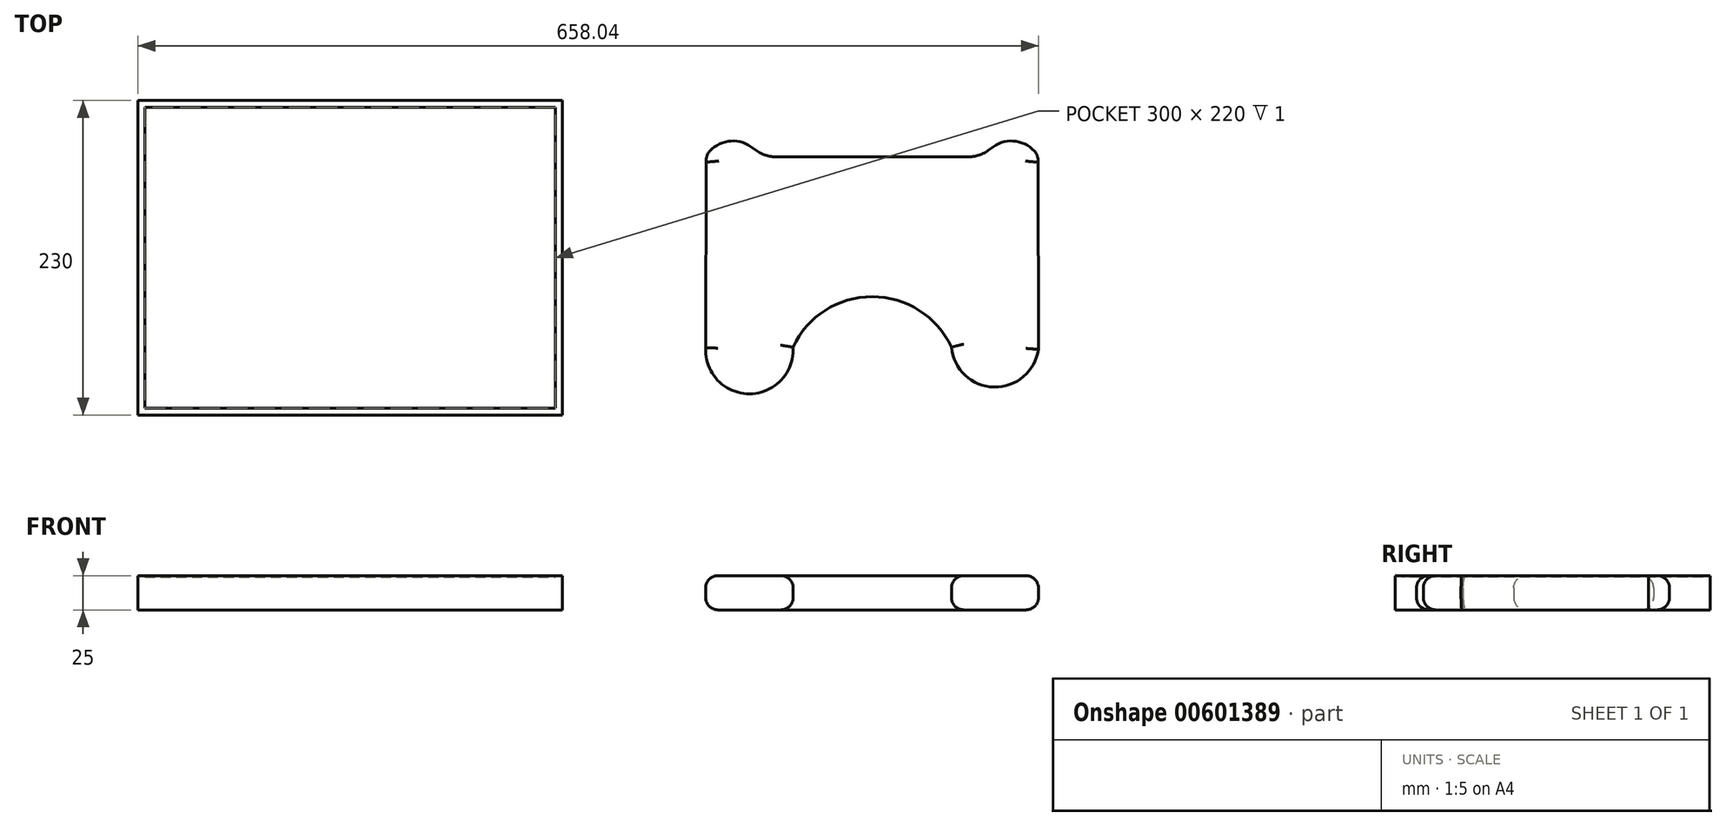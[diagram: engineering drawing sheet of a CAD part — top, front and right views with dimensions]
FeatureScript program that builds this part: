
annotation { "Feature Type Name" : "Feature", "Feature Type Description" : "" }
export const myFeature = defineFeature(function(context is Context, id is Id, definition is map)
    precondition{}
    {
        {
            var Q0;
            Q0=qCreatedBy(makeId("Top.planeOp"),FACE);
            var sketch = newSketch(context, id + "F0", { "sketchPlane" : qUnion([Q0])});
            skLineSegment(sketch, "E0.bottom", {"start": v(-155, 115) * mm, "end": v(155, 115) * mm});
            skLineSegment(sketch, "E0.top", {"start": v(-155, -115) * mm, "end": v(155, -115) * mm});
            skLineSegment(sketch, "E0.left", {"start": v(-155, 115) * mm, "end": v(-155, -115) * mm});
            skLineSegment(sketch, "E0.right", {"start": v(155, 115) * mm, "end": v(155, -115) * mm});
            skLineSegment(sketch, "E1", {"start": v(0, 0) * mm, "end": v(0, 115) * mm, "construction": true});
            skLineSegment(sketch, "E2", {"start": v(0, 0) * mm, "end": v(155, 0) * mm, "construction": true});
            skSolve(sketch);
        }
        {
            var Q0;
            Q0=makeQuery(id+"F0.imprint","IMPRINT",FACE,{"disambiguationData":[TD([[makeQuery(id+"F0.imprint","IMPRINT",EDGE,{"derivedFrom":sQuery(id+"F0.wireOp",EDGE,"E0.bottom")}),-1.0]])]});
            extrude(context, id + "F1", {"entities" : qUnion([Q0]), "depth" : 25 * mm, "offsetDistance" : 25 * mm, "symmetric" : true});
        }
        {
            var Q0;
            Q0=makeQuery(id+"F1.opExtrude","CAP_FACE",FACE,{"disambiguationData":[OSD([sQuery(id+"F0.wireOp",EDGE,"E0.bottom"),sQuery(id+"F0.wireOp",EDGE,"E0.top"),sQuery(id+"F0.wireOp",EDGE,"E0.left"),sQuery(id+"F0.wireOp",EDGE,"E0.right")])],"isStart":false});
            var sketch = newSketch(context, id + "F2", { "sketchPlane" : qUnion([Q0])});
            skLineSegment(sketch, "E3.bottom", {"start": v(-150, 110) * mm, "end": v(150, 110) * mm});
            skLineSegment(sketch, "E3.top", {"start": v(-150, -110) * mm, "end": v(150, -110) * mm});
            skLineSegment(sketch, "E3.left", {"start": v(-150, 110) * mm, "end": v(-150, -110) * mm});
            skLineSegment(sketch, "E3.right", {"start": v(150, 110) * mm, "end": v(150, -110) * mm});
            skSolve(sketch);
        }
        {
            var Q0;
            Q0=makeQuery(id+"F2.imprint","IMPRINT",FACE,{"disambiguationData":[TD([[makeQuery(id+"F2.imprint","IMPRINT",EDGE,{"derivedFrom":sQuery(id+"F2.wireOp",EDGE,"E3.bottom")}),-1.0]])]});
            extrude(context, id + "F3", {"entities" : qUnion([Q0]), "operationType" : NewBodyOperationType.REMOVE, "oppositeDirection" : true, "depth" : 1 * mm, "offsetDistance" : 25 * mm});
        }
        {
            var Q0;
            Q0=qCreatedBy(makeId("Top.planeOp"),FACE);
            var sketch = newSketch(context, id + "F4", { "sketchPlane" : qUnion([Q0])});
            skArc(sketch, "E4", {"start": v(259.83, -65.82) * mm, "mid": v(292, -99.5) * mm, "end": v(323.72, -65.41) * mm});
            skArc(sketch, "E5", {"start": v(439.47, -65.41) * mm, "mid": v(381.6, -28.43) * mm, "end": v(323.72, -65.41) * mm});
            skArc(sketch, "E6", {"start": v(439.47, -65.41) * mm, "mid": v(470.57, -94.54) * mm, "end": v(503.04, -66.95) * mm});
            skArc(sketch, "E7", {"start": v(294.87, 79.85) * mm, "mid": v(278.48, 85.39) * mm, "end": v(262.87, 77.94) * mm});
            skArc(sketch, "E8", {"start": v(500.1, 78.05) * mm, "mid": v(484.51, 85.4) * mm, "end": v(468.2, 79.85) * mm});
            skLineSegment(sketch, "E9", {"start": v(311.2, 73.79) * mm, "end": v(451.88, 73.79) * mm});
            skPoint(sketch, "E10.visualSharp", {"position": v(299.86, 73.79) * mm});
            skArc(sketch, "E10.filletArc", {"start": v(294.87, 79.85) * mm, "mid": v(302.49, 75.35) * mm, "end": v(311.2, 73.79) * mm});
            skPoint(sketch, "E11.visualSharp", {"position": v(463.21, 73.79) * mm});
            skArc(sketch, "E11.filletArc", {"start": v(451.88, 73.79) * mm, "mid": v(460.58, 75.35) * mm, "end": v(468.2, 79.85) * mm});
            skPoint(sketch, "E12.visualSharp", {"position": v(503.21, 73.79) * mm});
            skArc(sketch, "E12.filletArc", {"start": v(502.66, 69.9) * mm, "mid": v(502.3, 74.26) * mm, "end": v(500.1, 78.05) * mm});
            skPoint(sketch, "E13.visualSharp", {"position": v(259.86, 73.79) * mm});
            skArc(sketch, "E13.filletArc", {"start": v(262.87, 77.94) * mm, "mid": v(260.73, 74.24) * mm, "end": v(260.33, 70) * mm});
            skLineSegment(sketch, "E14", {"start": v(502.66, 69.9) * mm, "end": v(503.04, -66.95) * mm});
            skLineSegment(sketch, "E15", {"start": v(260.33, 70) * mm, "end": v(259.83, -65.82) * mm});
            skSolve(sketch);
        }
        {
            var Q0;
            Q0=makeQuery(id+"F4.imprint","IMPRINT",FACE,{"disambiguationData":[TD([[makeQuery(id+"F4.imprint","IMPRINT",EDGE,{"derivedFrom":sQuery(id+"F4.wireOp",EDGE,"E4")}),1.0]])]});
            extrude(context, id + "F5", {"entities" : qUnion([Q0]), "depth" : 25 * mm, "offsetDistance" : 25 * mm, "symmetric" : true});
        }
        {
            var Q0;
            Q0=makeQuery(id+"F5.opExtrude","CAP_EDGE",EDGE,{"disambiguationData":[OSD([sQuery(id+"F4.wireOp",EDGE,"E5")])],"isStart":false});
            var Q1;
            Q1=makeQuery(id+"F5.opExtrude","CAP_EDGE",EDGE,{"disambiguationData":[OSD([sQuery(id+"F4.wireOp",EDGE,"E5")])],"isStart":true});
            var Q2;
            Q2=makeQuery(id+"F5.opExtrude","CAP_EDGE",EDGE,{"disambiguationData":[OSD([sQuery(id+"F4.wireOp",EDGE,"E4")])],"isStart":true});
            var Q3;
            Q3=makeQuery(id+"F5.opExtrude","CAP_EDGE",EDGE,{"disambiguationData":[OSD([sQuery(id+"F4.wireOp",EDGE,"E4")])],"isStart":false});
            var Q4;
            Q4=makeQuery(id+"F5.opExtrude","CAP_EDGE",EDGE,{"disambiguationData":[OSD([sQuery(id+"F4.wireOp",EDGE,"E6")])],"isStart":false});
            var Q5;
            Q5=makeQuery(id+"F5.opExtrude","CAP_EDGE",EDGE,{"disambiguationData":[OSD([sQuery(id+"F4.wireOp",EDGE,"E9")])],"isStart":true});
            var Q6;
            Q6=makeQuery(id+"F5.opExtrude","CAP_EDGE",EDGE,{"disambiguationData":[OSD([sQuery(id+"F4.wireOp",EDGE,"E6")])],"isStart":true});
            var Q7;
            Q7=makeQuery(id+"F5.opExtrude","CAP_EDGE",EDGE,{"disambiguationData":[OSD([sQuery(id+"F4.wireOp",EDGE,"E14")])],"isStart":false});
            var Q8;
            Q8=makeQuery(id+"F5.opExtrude","CAP_EDGE",EDGE,{"disambiguationData":[OSD([sQuery(id+"F4.wireOp",EDGE,"E14")])],"isStart":true});
            var Q9;
            Q9=makeQuery(id+"F5.opExtrude","CAP_EDGE",EDGE,{"disambiguationData":[OSD([sQuery(id+"F4.wireOp",EDGE,"E8")])],"isStart":false});
            var Q10;
            Q10=makeQuery(id+"F5.opExtrude","CAP_EDGE",EDGE,{"disambiguationData":[OSD([sQuery(id+"F4.wireOp",EDGE,"E12.filletArc")])],"isStart":false});
            fillet(context, id + "F6", {"entities" : qUnion([Q0, Q1, Q2, Q3, Q4, Q5, Q6, Q7, Q8, Q9, Q10]), "radius" : 9 * mm, "tangentPropagation" : true, "allowEdgeOverflow" : false});
        }
    });
